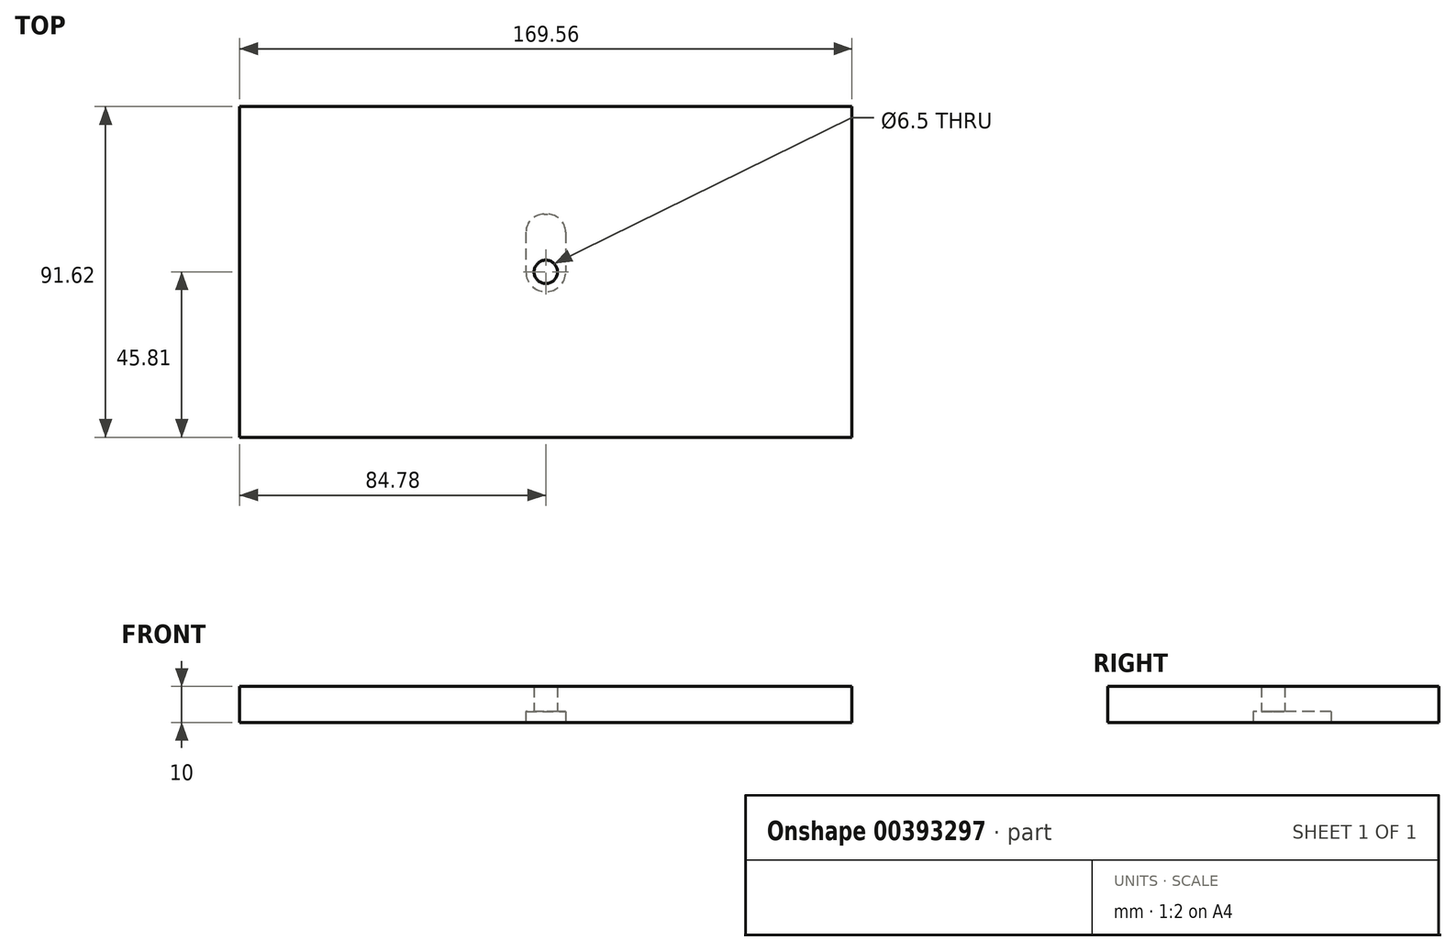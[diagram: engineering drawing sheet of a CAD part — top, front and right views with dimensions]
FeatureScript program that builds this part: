
annotation { "Feature Type Name" : "Feature", "Feature Type Description" : "" }
export const myFeature = defineFeature(function(context is Context, id is Id, definition is map)
    precondition{}
    {
        {
            var Q0;
            Q0=qCreatedBy(makeId("Top.planeOp"),FACE);
            var sketch = newSketch(context, id + "F0", { "sketchPlane" : qUnion([Q0])});
            skLineSegment(sketch, "E0.bottom", {"start": v(-84.78, 45.81) * mm, "end": v(84.78, 45.81) * mm});
            skLineSegment(sketch, "E0.top", {"start": v(-84.78, -45.81) * mm, "end": v(84.78, -45.81) * mm});
            skLineSegment(sketch, "E0.left", {"start": v(-84.78, 45.81) * mm, "end": v(-84.78, -45.81) * mm});
            skLineSegment(sketch, "E0.right", {"start": v(84.78, 45.81) * mm, "end": v(84.78, -45.81) * mm});
            skPoint(sketch, "E0.middle", {"position": v(0, 0) * mm});
            skCircle(sketch, "E1", {"center": v(0, 0) * mm, "radius": 3.25 * mm});
            skSolve(sketch);
        }
        {
            var Q0;
            Q0=makeQuery(id+"F0.imprint","IMPRINT",FACE,{"disambiguationData":[TD([[makeQuery(id+"F0.imprint","IMPRINT",EDGE,{"derivedFrom":sQuery(id+"F0.wireOp",EDGE,"E0.bottom")}),-1.0]])]});
            extrude(context, id + "F1", {"entities" : qUnion([Q0]), "depth" : 10 * mm, "offsetDistance" : 25 * mm});
        }
        {
            var Q0;
            Q0=makeQuery(id+"F0.imprint","IMPRINT",FACE,{"disambiguationData":[TD([[makeQuery(id+"F0.imprint","IMPRINT",EDGE,{"derivedFrom":sQuery(id+"F0.wireOp",EDGE,"E0.bottom")}),-1.0]])]});
            var sketch = newSketch(context, id + "F2", { "sketchPlane" : qUnion([Q0])});
            skCircle(sketch, "E2", {"center": v(0, 0) * mm, "radius": 5.5 * mm});
            skLineSegment(sketch, "E3", {"start": v(0, 16) * mm, "end": v(-5.5, 16) * mm});
            skLineSegment(sketch, "E4", {"start": v(-5.5, 16) * mm, "end": v(-5.5, 0) * mm});
            skLineSegment(sketch, "E5.MirrorCS", {"start": v(0, 16) * mm, "end": v(5.5, 16) * mm});
            skLineSegment(sketch, "E6.MirrorCS", {"start": v(5.5, 16) * mm, "end": v(5.5, 0) * mm});
            skCircle(sketch, "E7", {"center": v(0, 0) * mm, "radius": 3.25 * mm});
            skSolve(sketch);
        }
        {
            var Q0;
            Q0=makeQuery(id+"F2.imprint","IMPRINT",FACE,{"disambiguationData":[TD([[makeQuery(id+"F2.imprint","IMPRINT",EDGE,{"derivedFrom":sQuery(id+"F2.wireOp",EDGE,"E3")}),1.0]])]});
            var Q1;
            Q1=makeQuery(id+"F2.imprint","IMPRINT",FACE,{"disambiguationData":[TD([[makeQuery(id+"F2.imprint","IMPRINT",EDGE,{"derivedFrom":sQuery(id+"F2.wireOp",EDGE,"E7")}),-1.0]])]});
            extrude(context, id + "F3", {"entities" : qUnion([Q0, Q1]), "operationType" : NewBodyOperationType.REMOVE, "depth" : 3 * mm, "offsetDistance" : 25 * mm});
        }
        {
            var Q0;
            Q0=makeQuery(id+"F3.boolean.opBoolean","COPY",EDGE,{"derivedFrom":makeQuery(id+"F3.opExtrude","SWEPT_EDGE",EDGE,{"disambiguationData":[OSD([sQuery(id+"F2.wireOp",EDGE,"E5.MirrorCS"),sQuery(id+"F2.wireOp",EDGE,"E6.MirrorCS")])]})});
            var Q1;
            Q1=makeQuery(id+"F3.boolean.opBoolean","COPY",EDGE,{"derivedFrom":makeQuery(id+"F3.opExtrude","SWEPT_EDGE",EDGE,{"disambiguationData":[OSD([sQuery(id+"F2.wireOp",EDGE,"E3"),sQuery(id+"F2.wireOp",EDGE,"E4")])]})});
            fillet(context, id + "F4", {"entities" : qUnion([Q0, Q1]), "radius" : 5 * mm, "tangentPropagation" : true, "allowEdgeOverflow" : false});
        }
    });
